# Revit family: Projector_Screen-Draper-Access_Fit_E
name_source: partatom
category: Specialty Equipment
units: mm (PartAtom-declared; Revit-internal decimal feet)

## family parameters
Classification Number = 23.85.10.14.31
Cut with Voids When Loaded = No
Enable Cutting in Views = No
Host = Face
Maintain Annotation Orientation = No
Part Type = Normal
Room Calculation Point = No
Round Connector Dimension = Use Diameter
Shared = No

## types (27) — shared parameters
Apparent Load = 132 VA
Cap Height = 5 9/16"
Cap Width = 6 49/64"
Case Height = 5 1/8"
Case Material = Metal - Draper - Stainless Steel - Polished
Case Width = 6 7/16"
Default Elevation = 4' - 0"
Description = Projection Screen
Frequency = 60 Hz
Manufacturer = Draper Inc.
Model = Access Fit/Series E
Number of Poles = 1
Product Documentation Link = http://www.draperinc.com
Product Name = Access Fit/Series E  Electric Projection Screen
Product Page URL = http://www.draperinc.com
Projection Screen Material = Fabric - Draper - CH1900E - Pearl White
URL = http://www.draperinc.com
Voltage = 110 V
Width = 8 25/128"

## per-type parameters (varying)
| type | Image Area | Image Height | Image Width | Length | Overall Size | Screen Drop | Screen Height | Screen Width |
| AV Format  10 Feet  x 10 Feet | 10' x 10' | 9' - 8" | 9' - 8" | 11' - 4" | 10' x 10' | 10' - 0" | 10' - 0" | 10' - 0" |
| AV Format  8 Feet x 10 Feet | 8' x 10' | 7' - 8" | 9' - 8" | 11' - 4" | 8' x 10' | 8' - 0" | 8' - 0" | 10' - 0" |
| AV Format  9 Feet x 9 Feet | 9' x 9' | 8' - 8" | 8' - 8" | 10' - 6" | 9' x 9' | 9' - 0" | 9' - 0" | 9' - 0" |
| AV Format  7 Feet x 9 Feet | 7' x 9' | 6' - 8" | 8' - 8" | 10' - 6" | 7' x 9' | 7' - 0" | 7' - 0" | 9' - 0" |
| AV Format  96 Inches x 96 Inches | 96" x 96" | 7' - 8" | 7' - 8" | 9' - 5" | 96" x 96" | 8' - 0" | 8' - 0" | 8' - 0" |
| AV Format  72 Inches x 96 Inches | 72" x 96" | 5' - 8" | 7' - 8" | 9' - 5" | 72" x 96" | 6' - 0" | 6' - 0" | 8' - 0" |
| AV Format  84 Inches x 84 Inches | 84" x 84" | 6' - 8" | 6' - 8" | 8' - 6" | 84" x 84" | 7' - 0" | 7' - 0" | 7' - 0" |
| AV Format  70 Inches x 70 Inches | 70" x 70" | 5' - 6" | 5' - 6" | 7' - 1" | 70" x 70" | 5' - 10" | 5' - 10" | 5' - 10" |
| AV Format  60 Inches x 60 Inches | 60" x 60" | 4' - 8" | 4' - 8" | 6' - 4" | 60" x 60" | 5' - 0" | 5' - 0" | 5' - 0" |
| AV Format  50 Inches x 50 Inches | 50" x 50" | 3' - 10" | 3' - 10" | 5' - 6" | 50" x 50" | 4' - 2" | 4' - 2" | 4' - 2" |
| 16:10 Format 137 Inches | 72 1/2" x 116" | 6' - 0 1/2" | 9' - 8" | 11' - 4" | 76 1/2" x 120" | 6' - 4 1/2" | 6' - 4 1/2" | 10' - 0" |
| 16:10 Format 123 Inches | 65" x 104" | 5' - 5" | 8' - 8" | 10' - 6" | 69" x 108" | 5' - 9" | 5' - 9" | 9' - 0" |
| 16:10 Format 113 Inches | 60" x 96" | 5' - 8" | 8' - 0" | 9' - 11" | 72" x 100" | 6' - 0" | 6' - 0" | 8' - 4" |
| 16:10 Format 109 Inches | 57 1/2" x 92" | 5' - 5 1/2" | 7' - 8" | 9' - 5" | 69 1/2" x 96" | 5' - 9 1/2" | 5' - 9 1/2" | 8' - 0" |
| 16:10 Format 94 Inches | 50" x 80" | 4' - 10" | 6' - 7 1/2" | 8' - 6" | 62" x 83 1/2" | 5' - 2" | 5' - 2" | 6' - 11 1/2" |
| HDTV Format 133 Inches | 65" x 116" | 5' - 5" | 9' - 8" | 11' - 4" | 69" x 120" | 5' - 9" | 5' - 9" | 10' - 0" |
| HDTV Format 119 Inches | 58" x 104" | 4' - 10" | 8' - 8" | 10' - 6" | 62" x 108" | 5' - 2" | 5' - 2" | 9' - 0" |
| HDTV Format 110 Inches | 54" x 96" | 5' - 2" | 8' - 0" | 9' - 11" | 66" x 100" | 5' - 6" | 5' - 6" | 8' - 4" |
| HDTV Format 106 Inches | 52" x 92" | 5' - 0" | 7' - 8" | 9' - 5" | 64" x 96" | 5' - 4" | 5' - 4" | 8' - 0" |
| HDTV Format 100 Inches | 49" x 87" | 4' - 9" | 7' - 3" | 8' - 11" | 61" x 91" | 5' - 1" | 5' - 1" | 7' - 7" |
| HDTV Format 92 Inches | 45" x 80" | 4' - 5" | 6' - 7 1/2" | 8' - 6" | 57" x 83 1/2" | 4' - 9" | 4' - 9" | 6' - 11 1/2" |
| NTSC Video Format 150 Inches | 87" x 116" | 7' - 4" | 9' - 8" | 11' - 4" | 92" x 120" | 7' - 8" | 7' - 8" | 10' - 0" |
| NTSC Video Format 11 Feet | 78" x 104" | 6' - 7" | 8' - 8" | 10' - 6" | 83" x 108" | 6' - 11" | 6' - 11" | 9' - 0" |
| NTSC Video Format 10 Feet | 72" x 96" | 5' - 9" | 7' - 8" | 9' - 5" | 73" x 96" | 6' - 1" | 6' - 1" | 8' - 0" |
| NTSC Video Format 100 Inches | 60" x 80" | 5' - 0" | 6' - 7 1/2" | 8' - 6" | 64" x 83 1/2" | 5' - 4" | 5' - 4" | 6' - 11 1/2" |
| NTSC Video Format 7 Feet | 50" x 66 1/2" | 4' - 1 1/2" | 5' - 5 1/2" | 7' - 1" | 53 1/2" x 69 1/2" | 4' - 5 1/2" | 4' - 5 1/2" | 5' - 9 1/2" |
| NTSC Video Format 6 Feet | 42 1/2" x 56 1/2" | 3' - 6 1/2" | 4' - 7 1/2" | 6' - 4" | 46 1/2" x 59 1/2" | 3' - 10 1/2" | 3' - 10 1/2" | 4' - 11 1/2" |

## geometry (parser evidence)
native form markers: Blend x4, Sweep x2
no freeform markers — native parametric forms only
